# Revit family: Lighting_Outside_Zero_Convex_Pole-Fixture_Outside
name_source: partatom
category: Lighting Fixtures
units: mm (PartAtom-declared; Revit-internal decimal feet)

## family parameters
Always vertical = Yes
Cut with Voids When Loaded = No
Light Source = Yes
OmniClass Number = 23.80.70.00
OmniClass Title = Lighting
Part Type = Normal
Room Calculation Point = No
Round Connector Dimension = Use Diameter
Shared = No
Work Plane-Based = No

## types (6) — shared parameters
AssetType = Fixed
BIMObjectName = Lighting_Outside_Zero_Convex_Pole-Fixture_Outside
Brand = Zero
Category = Pole Fixture
Collection = Convex
Color = Grey
Color Filter = 16777215
ColourIndexRA = >80
Dimming Lamp Color Temperature Shift = <None>
DurationUnit = Year
Features = Cable with quick connection inside the pole
HasProtectiveEarth = No
IK Classification = 08
IP_Code = IP44
IfcExportAs = IfcLightFixtureType
IfcExportType = NOTDEFINED
LensMaterial = Tempered glass
LightFixtureMainMaterial = Steel, Galvanized
LightFixtureMountingType = Surface
LightFixturePlacingType = Floor
Manufacturer = Zero
ManufacturerName = Zero
ManufacturerURL = https://www.zerolighting.com
Material = Steel & glass
NBSDescription = General purpose luminaires
NBSReference = 90-60-50/405
Name = Zero_Convex_Pole-Fixture_Outside
NominalCurrent = 0 A
NominalDiameter = 280 mm  [stored 0.918635 ft]
NominalFrequencyRange = 50 Hz
NominalHeight = 309 mm
NominalLength = 506 mm
NominalRadius = 140 mm  [stored 0.459318 ft]
NominalVoltage = 230 V
NominalVoltageCalc = 0 V
NominalWidth = 280 mm  [stored 0.918635 ft]
NumberOfPoles = 1
PhaseAngle = 0.00°
ProductDatasheet = https://www.zerolighting.com
Revision = 5
Shape = Cone
Size = 450x280x278 mm
Tilt Angle = 14.00°
TotalWattage = 32 W
URL = https://www.zerolighting.com
Uniclass2 = Pr_70_70_48_32
Uniclass2015Description = Free standing luminaires
Uniclass2015Reference = Pr_70_70_48_32
UsageCurrent = 0 A
Version = 3
VersionDate = 31/08/2023
WarrantyDurationUnit = Year
zero-valued in all types: Default Elevation, DefaultElevation, ElectricalDeviceNominalPower, MaintenanceFactor, NumberOfSources

## per-type parameters (varying)
| type | ArticleNumber | Dimming | Finish | ModelNumber | Photometric Web File |
| Convex pole LED 1940/32W Asymmetrical Dimmable DALI | 8294-1-83HFF | Dimmable DALI | Galvanized metal. Tempered glass. Asymmetrical light beam. | 8294-1-83HFF | Convex82941.IES |
| Convex pole LED 1940/32W Asymmetrical | 8294-1-83 |  | Galvanized metal. Tempered glass. Asymmetrical light beam. | 8294-1-83 | Convex82941.IES |
| Convex pole LED 1940/32W Asymmetrical Night-time dimming | 8294-1-83N | Night-time dimming | Galvanized metal. Tempered glass. Asymmetrical light beam. | 8294-1-83N | Convex82941.IES |
| Convex pole LED 1920/32W Comfort | 8295-1-83 |  | Galvanized metal. Tempered glass. Symmetrical light beam. | 8295-1-83 | Convex82931.IES |
| Convex pole LED 1920/32W Comfort Dimmable DALI | 8295-1-83HFF | Dimmable DALI | Galvanized metal. Tempered glass. Symmetrical light beam. | 8295-1-83HFF | Convex82931.IES |
| Convex pole LED 1920/32W Comfort Night-time dimming | 8295-1-83N | Night-time dimming | Galvanized metal. Tempered glass. Symmetrical light beam. | 8295-1-83N | Convex82931.IES |

note: column(s) folded — value = type name in every type: Model

note: [stored X ft] marks values corroborated as IEEE doubles in the binary element streams (Revit-internal decimal feet)

## geometry (parser evidence)
native form markers: Sweep x5
no freeform markers — native parametric forms only
